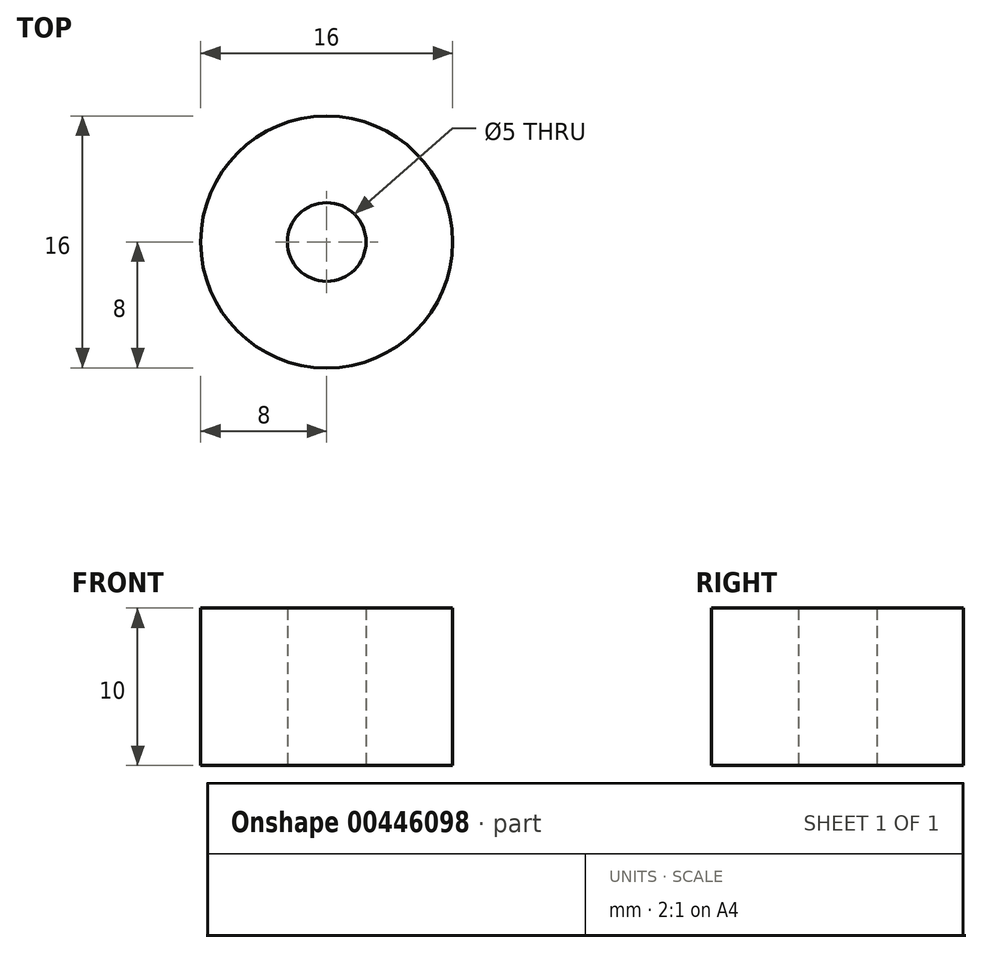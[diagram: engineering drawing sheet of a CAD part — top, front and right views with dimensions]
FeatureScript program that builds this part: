
annotation { "Feature Type Name" : "Feature", "Feature Type Description" : "" }
export const myFeature = defineFeature(function(context is Context, id is Id, definition is map)
    precondition{}
    {
        {
            var Q0;
            Q0=qCreatedBy(makeId("Top.planeOp"),FACE);
            var sketch = newSketch(context, id + "F0", { "sketchPlane" : qUnion([Q0])});
            skCircle(sketch, "E0", {"center": v(0, 0) * mm, "radius": 2.5 * mm});
            skCircle(sketch, "E1", {"center": v(0, 0) * mm, "radius": 8 * mm});
            skSolve(sketch);
        }
        {
            var Q0;
            Q0 = qSketchRegion(id + "F0", true);
            extrude(context, id + "F1", {"entities" : qUnion([Q0]), "depth" : 10 * mm, "offsetDistance" : 25 * mm});
        }
    });
